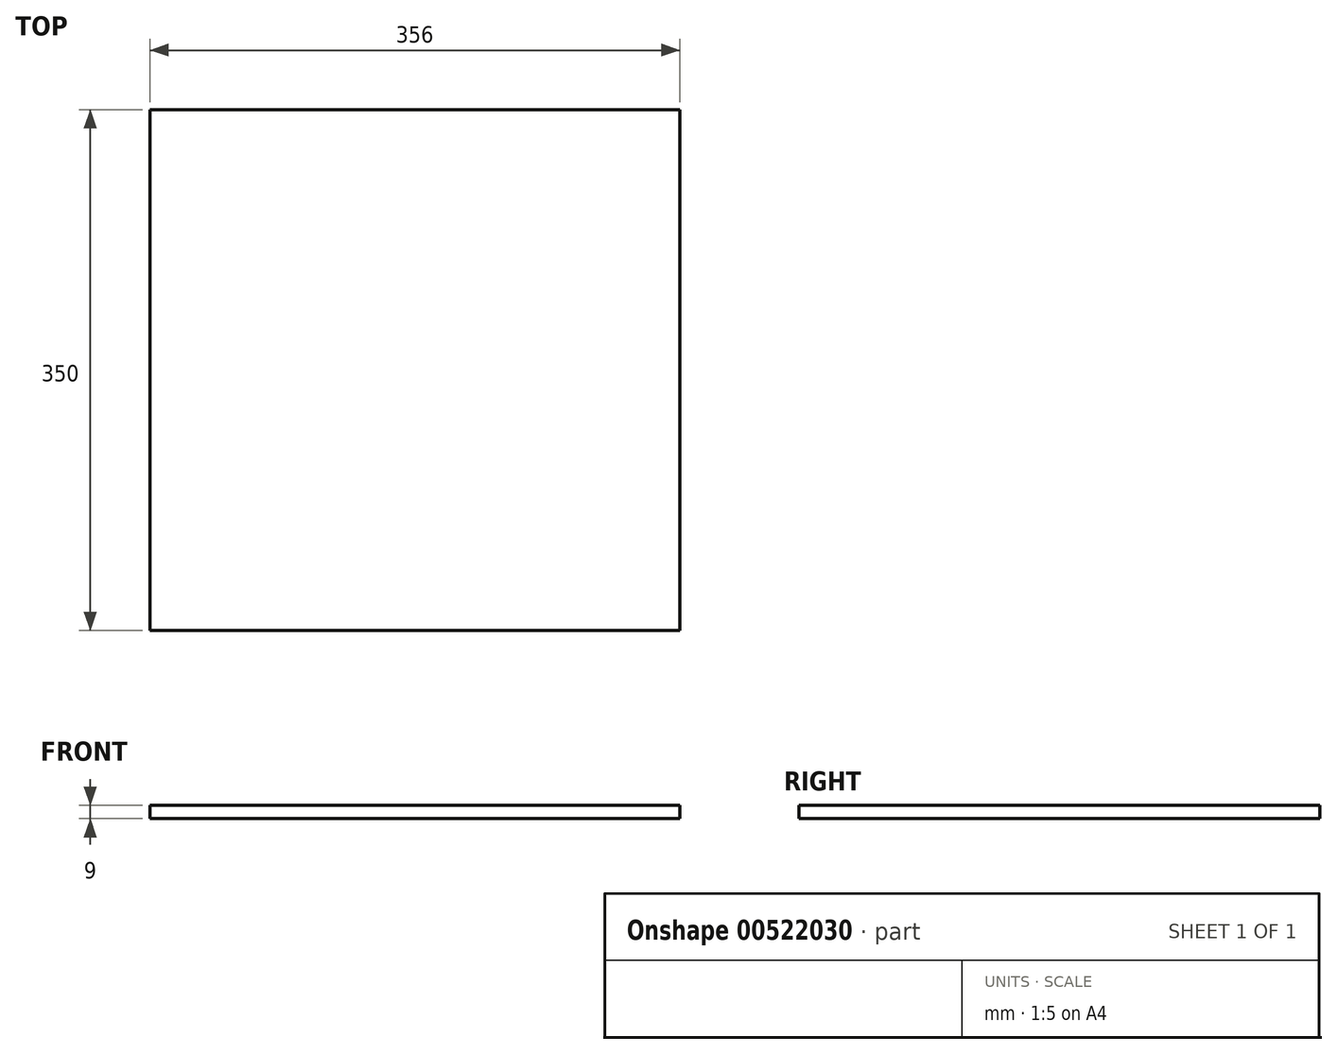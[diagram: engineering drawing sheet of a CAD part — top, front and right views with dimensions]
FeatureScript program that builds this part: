
annotation { "Feature Type Name" : "Feature", "Feature Type Description" : "" }
export const myFeature = defineFeature(function(context is Context, id is Id, definition is map)
    precondition{}
    {
        {
            var Q0;
            Q0=qCreatedBy(makeId("Top.planeOp"),FACE);
            var sketch = newSketch(context, id + "F0", { "sketchPlane" : qUnion([Q0])});
            skLineSegment(sketch, "E0.bottom", {"start": v(0, 0) * mm, "end": v(356, 0) * mm});
            skLineSegment(sketch, "E0.top", {"start": v(0, 350) * mm, "end": v(356, 350) * mm});
            skLineSegment(sketch, "E0.left", {"start": v(0, 0) * mm, "end": v(0, 350) * mm});
            skLineSegment(sketch, "E0.right", {"start": v(356, 0) * mm, "end": v(356, 350) * mm});
            skSolve(sketch);
        }
        {
            var Q0;
            Q0=makeQuery(id+"F0.imprint","IMPRINT",FACE,{"disambiguationData":[TD([[makeQuery(id+"F0.imprint","IMPRINT",EDGE,{"derivedFrom":sQuery(id+"F0.wireOp",EDGE,"E0.bottom")}),1.0]])]});
            extrude(context, id + "F1", {"entities" : qUnion([Q0]), "depth" : 9 * mm, "offsetDistance" : 25 * mm});
        }
    });
